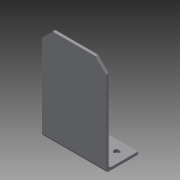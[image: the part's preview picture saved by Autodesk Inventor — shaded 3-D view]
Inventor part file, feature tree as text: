
AUTODESK INVENTOR PART (.ipt)
format: ipt  version: 2015 SP1 (Build 190203100, 203)  size: 97,280 bytes
history: native  units: in
note: dims shown in document units (in); Inventor stores cm internally (conversion verified against a paired STEP export)
features: sketch x2, extrude x1, hole x1, fillet x1, chamfer x1
ambient origin geometry x8: Origin, YZ Plane, XZ Plane, XY Plane, X Axis, Y Axis, Z Axis, Center Point
bodies: Solid1 (feature_tree)
feature tree (6):
  extrude  "Extrusion1"  Depth=0.125in
  hole  "Hole1"  [1 undecoded]
  fillet  "Fillet1"  Radius=3.0in
  chamfer  "Chamfer1"  Distance=0.5in
  sketch  "Sketch1"  dims[d0=4.5in d1=0.125in]
  sketch  "Sketch2"  dims[d2=0.125in d3=1.25in d4=3.0in d5=0.0in d6=0.5in d7=0.5in d8=0.5in d9=0.5in d10=0.25in d11=0.75in d12=0.375in d13=0.25in d14=0.5635in d15=1.0in d16=0.8108in d17=0.125in d18=0.5in d19=0.125in d20=45.0deg]
note: 1 required parameter value undecoded (feature->parameter linkage not recoverable at this tier; creation-order binding heuristic only, values carry confidence <= 0.55)
